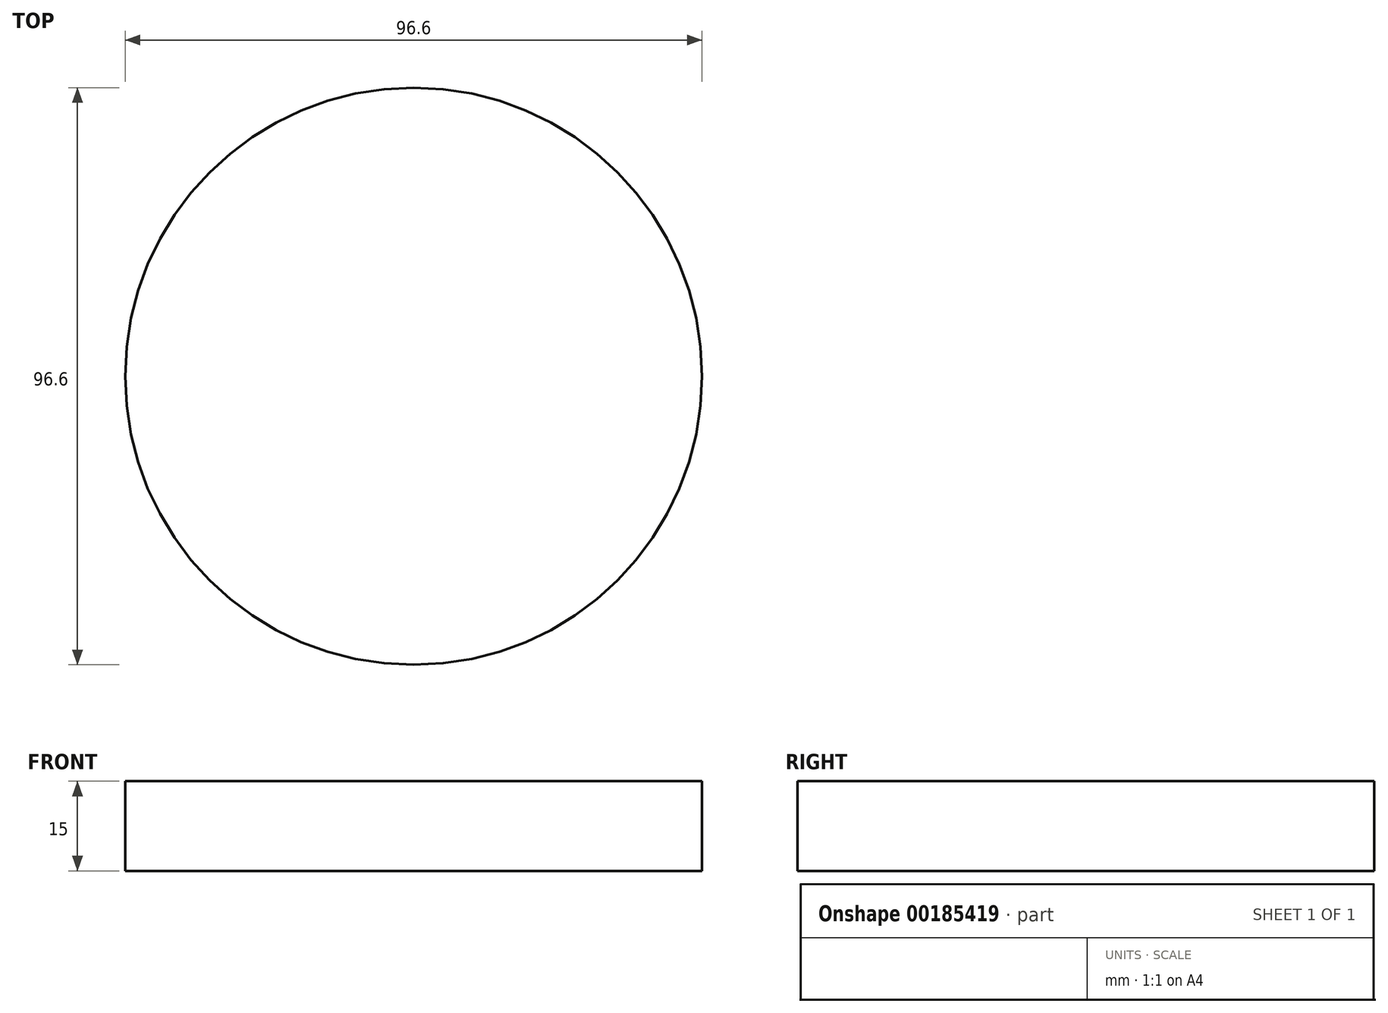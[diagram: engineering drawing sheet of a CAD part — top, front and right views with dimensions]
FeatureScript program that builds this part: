
annotation { "Feature Type Name" : "Feature", "Feature Type Description" : "" }
export const myFeature = defineFeature(function(context is Context, id is Id, definition is map)
    precondition{}
    {
        {
            var Q0;
            Q0=qCreatedBy(makeId("Top.planeOp"),FACE);
            var sketch = newSketch(context, id + "F0", { "sketchPlane" : qUnion([Q0])});
            skCircle(sketch, "E0", {"center": v(0, 0) * mm, "radius": 48.3 * mm});
            skSolve(sketch);
        }
        {
            var Q0;
            Q0=sQuery(id+"F0.wireOp",EDGE,"E0");
            extrude(context, id + "F1", {"bodyType" : ExtendedToolBodyType.SURFACE, "surfaceEntities" : qUnion([Q0]), "depth" : 15 * mm});
        }
    });
